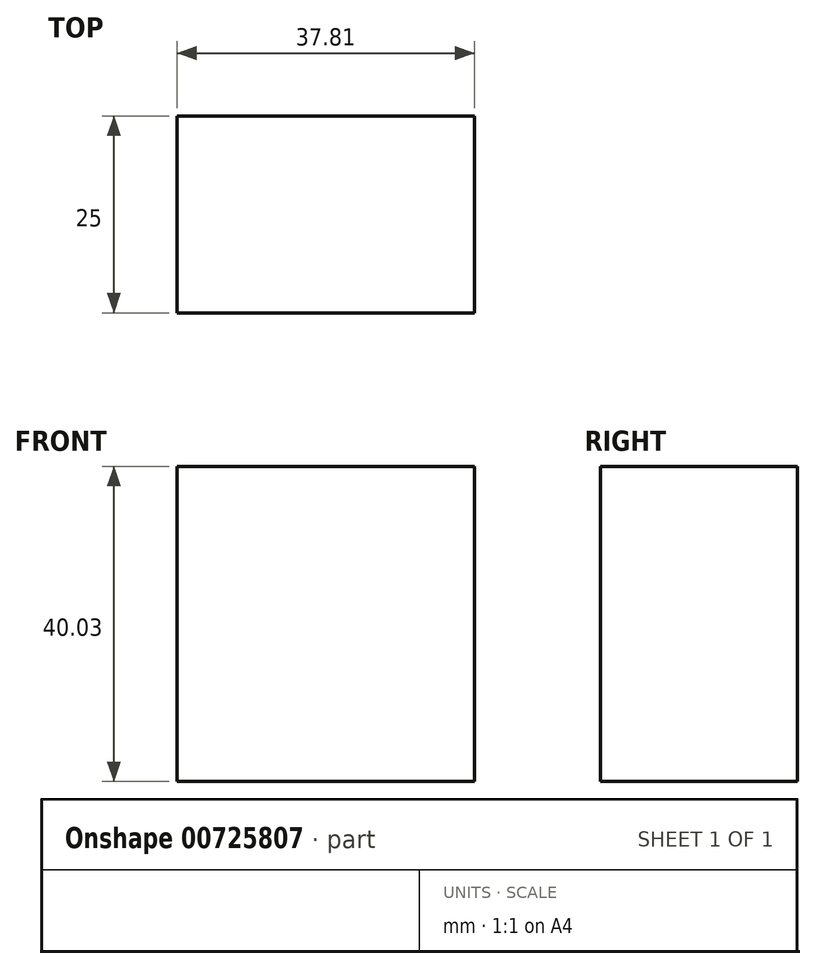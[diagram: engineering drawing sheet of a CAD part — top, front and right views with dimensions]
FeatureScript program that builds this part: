
annotation { "Feature Type Name" : "Feature", "Feature Type Description" : "" }
export const myFeature = defineFeature(function(context is Context, id is Id, definition is map)
    precondition{}
    {
        {
            var Q0;
            Q0=qCreatedBy(makeId("Front.planeOp"),FACE);
            var sketch = newSketch(context, id + "F0", { "sketchPlane" : qUnion([Q0])});
            skLineSegment(sketch, "E0.bottom", {"start": v(-53, 0) * mm, "end": v(-15.19, 0) * mm});
            skLineSegment(sketch, "E0.top", {"start": v(-53, 40.03) * mm, "end": v(-15.19, 40.03) * mm});
            skLineSegment(sketch, "E0.left", {"start": v(-53, 0) * mm, "end": v(-53, 40.03) * mm});
            skLineSegment(sketch, "E0.right", {"start": v(-15.19, 0) * mm, "end": v(-15.19, 40.03) * mm});
            skSolve(sketch);
        }
        {
            var Q0;
            Q0=makeQuery(id+"F0.imprint","IMPRINT",FACE,{"disambiguationData":[TD([[makeQuery(id+"F0.imprint","IMPRINT",EDGE,{"derivedFrom":sQuery(id+"F0.wireOp",EDGE,"E0.bottom")}),1.0]])]});
            extrude(context, id + "F1", {"entities" : qUnion([Q0]), "depth" : 25 * mm, "offsetDistance" : 25 * mm});
        }
    });
